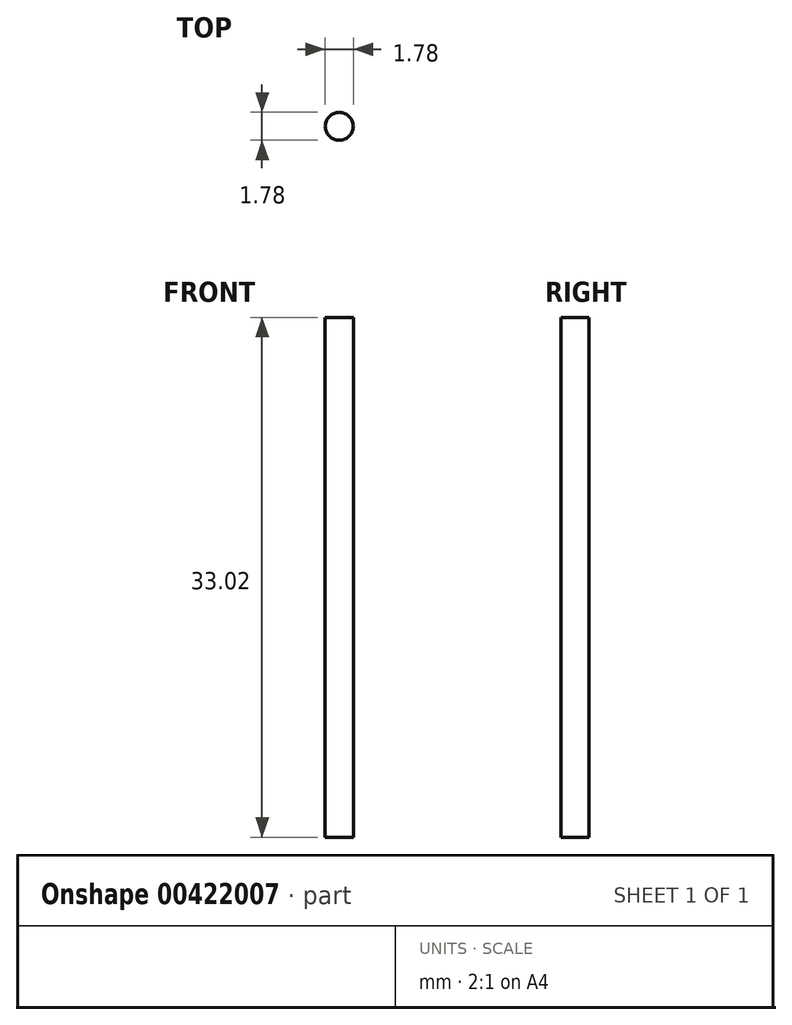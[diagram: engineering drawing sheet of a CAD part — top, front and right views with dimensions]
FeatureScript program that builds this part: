
annotation { "Feature Type Name" : "Feature", "Feature Type Description" : "" }
export const myFeature = defineFeature(function(context is Context, id is Id, definition is map)
    precondition{}
    {
        {
            var Q0;
            Q0=qCreatedBy(makeId("Top.planeOp"),FACE);
            var sketch = newSketch(context, id + "F0", { "sketchPlane" : qUnion([Q0])});
            skCircle(sketch, "E0", {"center": v(0, 0) * mm, "radius": 0.89 * mm});
            skSolve(sketch);
        }
        {
            var Q0;
            Q0=makeQuery(id+"F0.imprint","IMPRINT",FACE,{"disambiguationData":[TD([[makeQuery(id+"F0.imprint","IMPRINT",EDGE,{"derivedFrom":sQuery(id+"F0.wireOp",EDGE,"E0")}),1.0]])]});
            extrude(context, id + "F1", {"entities" : qUnion([Q0]), "depth" : 33.02 * mm});
        }
    });
